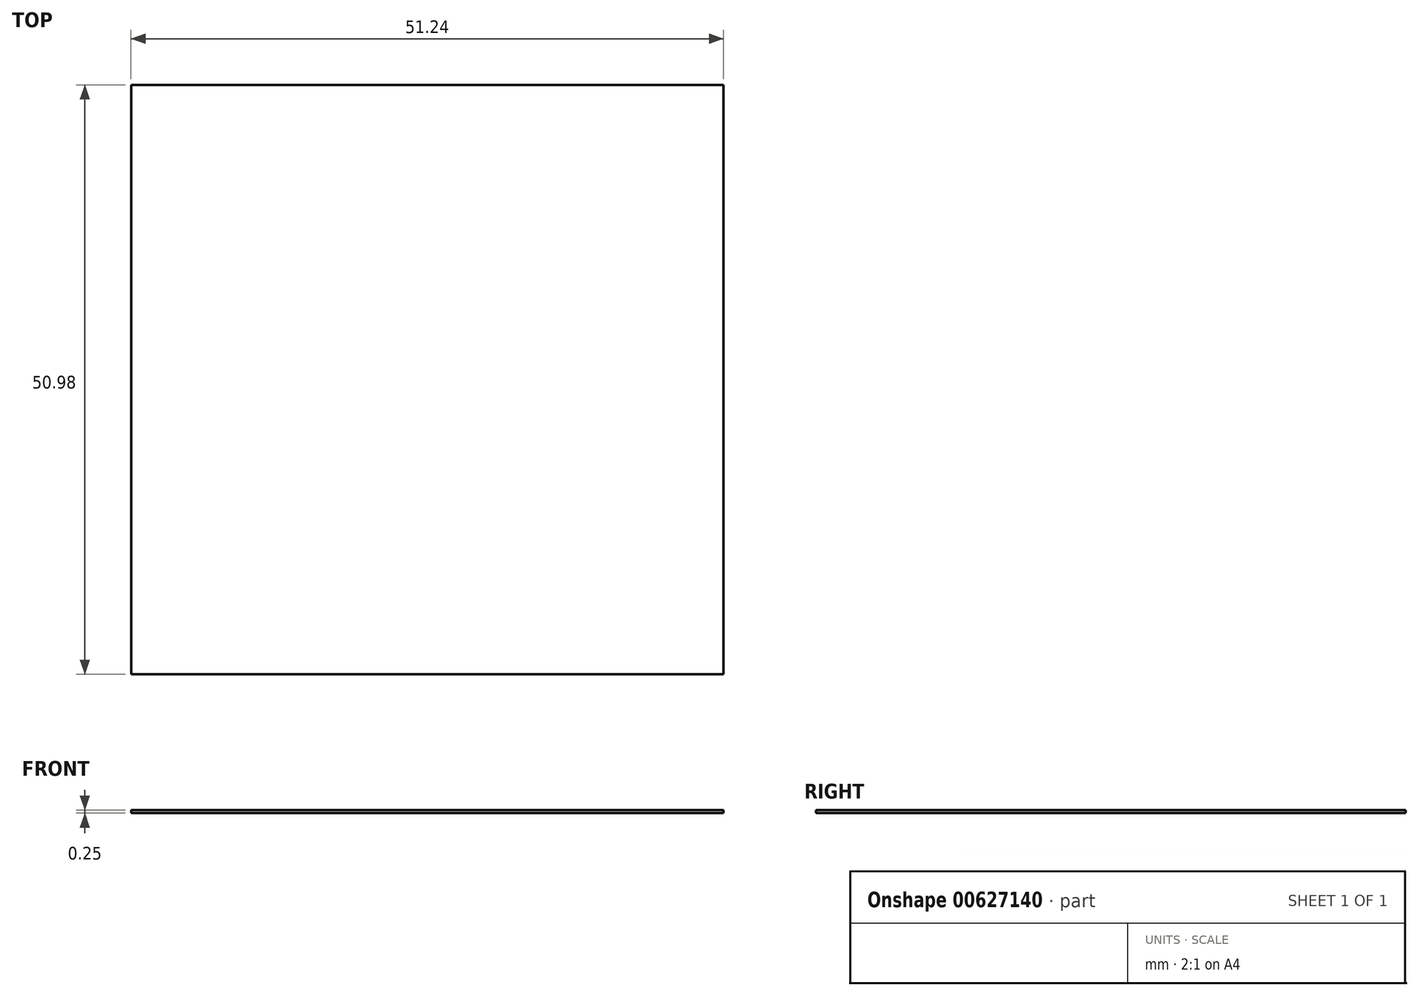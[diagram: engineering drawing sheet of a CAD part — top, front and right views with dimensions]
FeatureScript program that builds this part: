
annotation { "Feature Type Name" : "Feature", "Feature Type Description" : "" }
export const myFeature = defineFeature(function(context is Context, id is Id, definition is map)
    precondition{}
    {
        {
            var Q0;
            Q0=qCreatedBy(makeId("Top.planeOp"),FACE);
            var sketch = newSketch(context, id + "F0", { "sketchPlane" : qUnion([Q0])});
            skLineSegment(sketch, "E0.bottom", {"start": v(-25.62, -25.49) * mm, "end": v(25.62, -25.49) * mm});
            skLineSegment(sketch, "E0.top", {"start": v(-25.62, 25.49) * mm, "end": v(25.62, 25.49) * mm});
            skLineSegment(sketch, "E0.left", {"start": v(-25.62, -25.49) * mm, "end": v(-25.62, 25.49) * mm});
            skLineSegment(sketch, "E0.right", {"start": v(25.62, -25.49) * mm, "end": v(25.62, 25.49) * mm});
            skPoint(sketch, "E0.middle", {"position": v(0, 0) * mm});
            skSolve(sketch);
        }
        {
            var Q0;
            Q0 = qSketchRegion(id + "F0", true);
            extrude(context, id + "F1", {"entities" : qUnion([Q0]), "depth" : 0.25 * mm, "offsetDistance" : 25.4 * mm});
        }
    });
